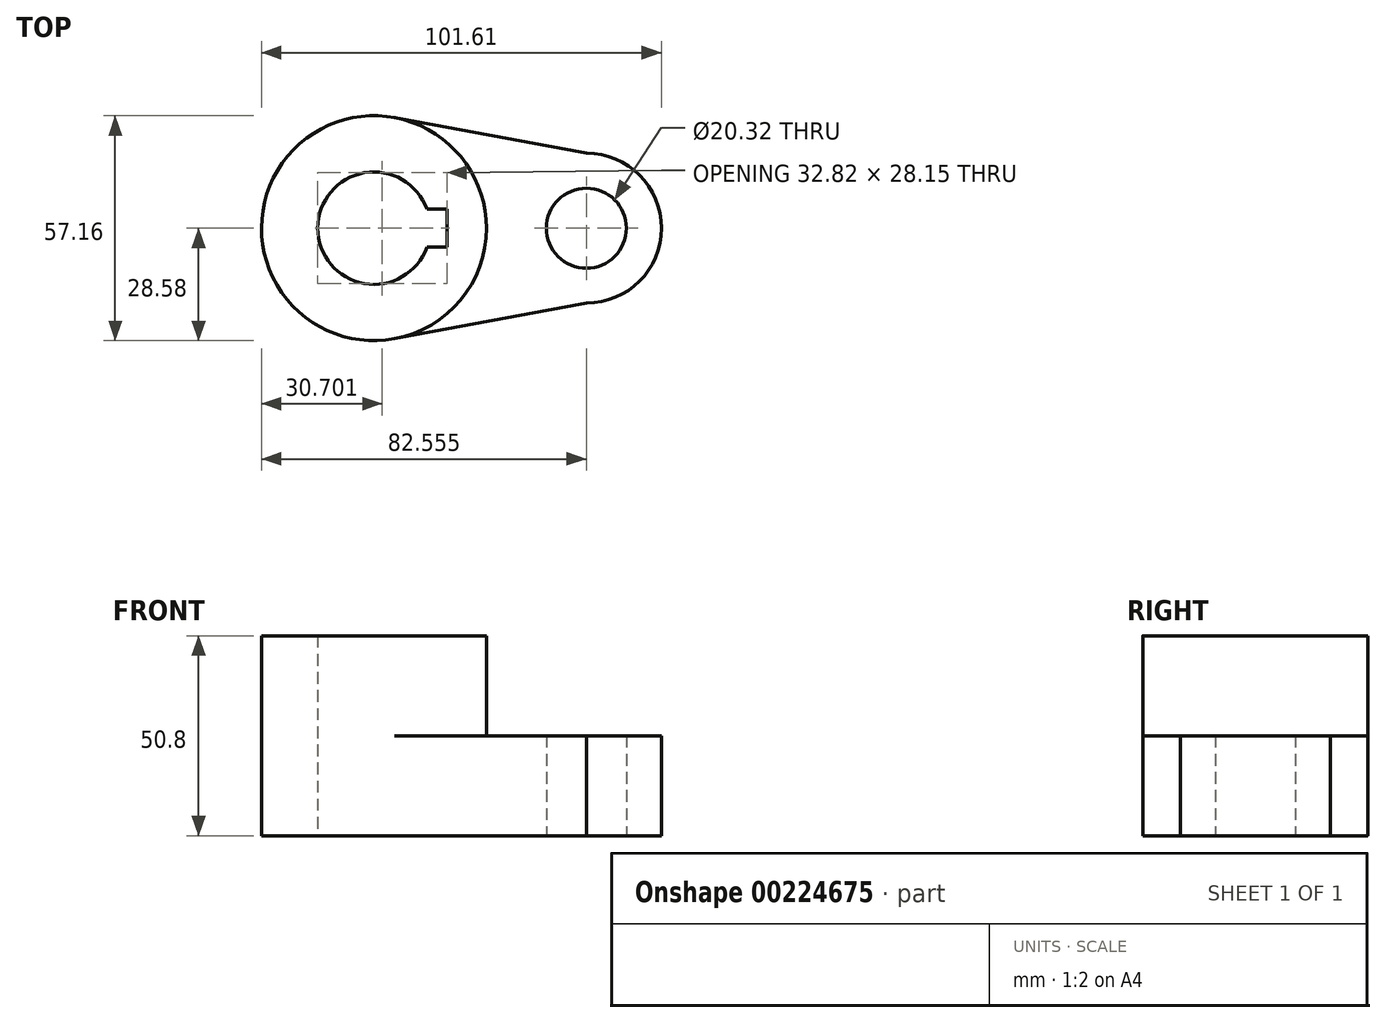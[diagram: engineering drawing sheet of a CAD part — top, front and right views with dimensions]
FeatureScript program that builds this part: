
annotation { "Feature Type Name" : "Feature", "Feature Type Description" : "" }
export const myFeature = defineFeature(function(context is Context, id is Id, definition is map)
    precondition{}
    {
        {
            var Q0;
            Q0=qCreatedBy(makeId("Top.planeOp"),FACE);
            var sketch = newSketch(context, id + "F0", { "sketchPlane" : qUnion([Q0])});
            skCircle(sketch, "E0", {"center": v(0, 0) * mm, "radius": 14.29 * mm});
            skCircle(sketch, "E1", {"center": v(0, 0) * mm, "radius": 28.58 * mm});
            skCircle(sketch, "E2", {"center": v(53.98, 0) * mm, "radius": 10.16 * mm});
            skArc(sketch, "E3", {"start": v(53.98, 19.05) * mm, "mid": v(73.03, 0) * mm, "end": v(53.98, -19.05) * mm});
            skLineSegment(sketch, "E4", {"start": v(53.97, 19.05) * mm, "end": v(0, 29.06) * mm});
            skLineSegment(sketch, "E5", {"start": v(53.97, -19.05) * mm, "end": v(0, -29.06) * mm});
            skLineSegment(sketch, "E6.bottom", {"start": v(-18.53, 4.83) * mm, "end": v(18.53, 4.83) * mm});
            skLineSegment(sketch, "E6.top", {"start": v(-18.53, -4.83) * mm, "end": v(18.53, -4.83) * mm});
            skLineSegment(sketch, "E6.left", {"start": v(-18.53, 4.83) * mm, "end": v(-18.53, -4.83) * mm});
            skLineSegment(sketch, "E6.right", {"start": v(18.53, 4.83) * mm, "end": v(18.53, -4.83) * mm});
            skSolve(sketch);
        }
        {
            var Q0;
            Q0=makeQuery(id+"F0.imprint","IMPRINT",FACE,{"disambiguationData":[TD([[makeQuery(id+"F0.imprint","IMPRINT",EDGE,{"derivedFrom":sQuery(id+"F0.wireOp",EDGE,"E2")}),-1.0]])]});
            extrude(context, id + "F1", {"entities" : qUnion([Q0]), "depth" : 25.4 * mm});
        }
        {
            var Q0;
            {var subQ7=sQuery(id+"F0.wireOp",EDGE,"E6.left");Q0=makeQuery(id+"F0.imprint","IMPRINT",FACE,{"disambiguationData":[TD([[makeQuery(id+"F0.imprint","IMPRINT",EDGE,{"derivedFrom":subQ7}),-1.0]])]});}
            var Q1;
            {var subQ5=sQuery(id+"F0.wireOp",EDGE,"E6.left");Q1=makeQuery(id+"F0.imprint","IMPRINT",FACE,{"disambiguationData":[TD([[makeQuery(id+"F0.imprint","IMPRINT",EDGE,{"derivedFrom":subQ5}),1.0]])]});}
            extrude(context, id + "F2", {"entities" : qUnion([Q0, Q1]), "operationType" : NewBodyOperationType.ADD, "depth" : 50.8 * mm});
        }
    });
